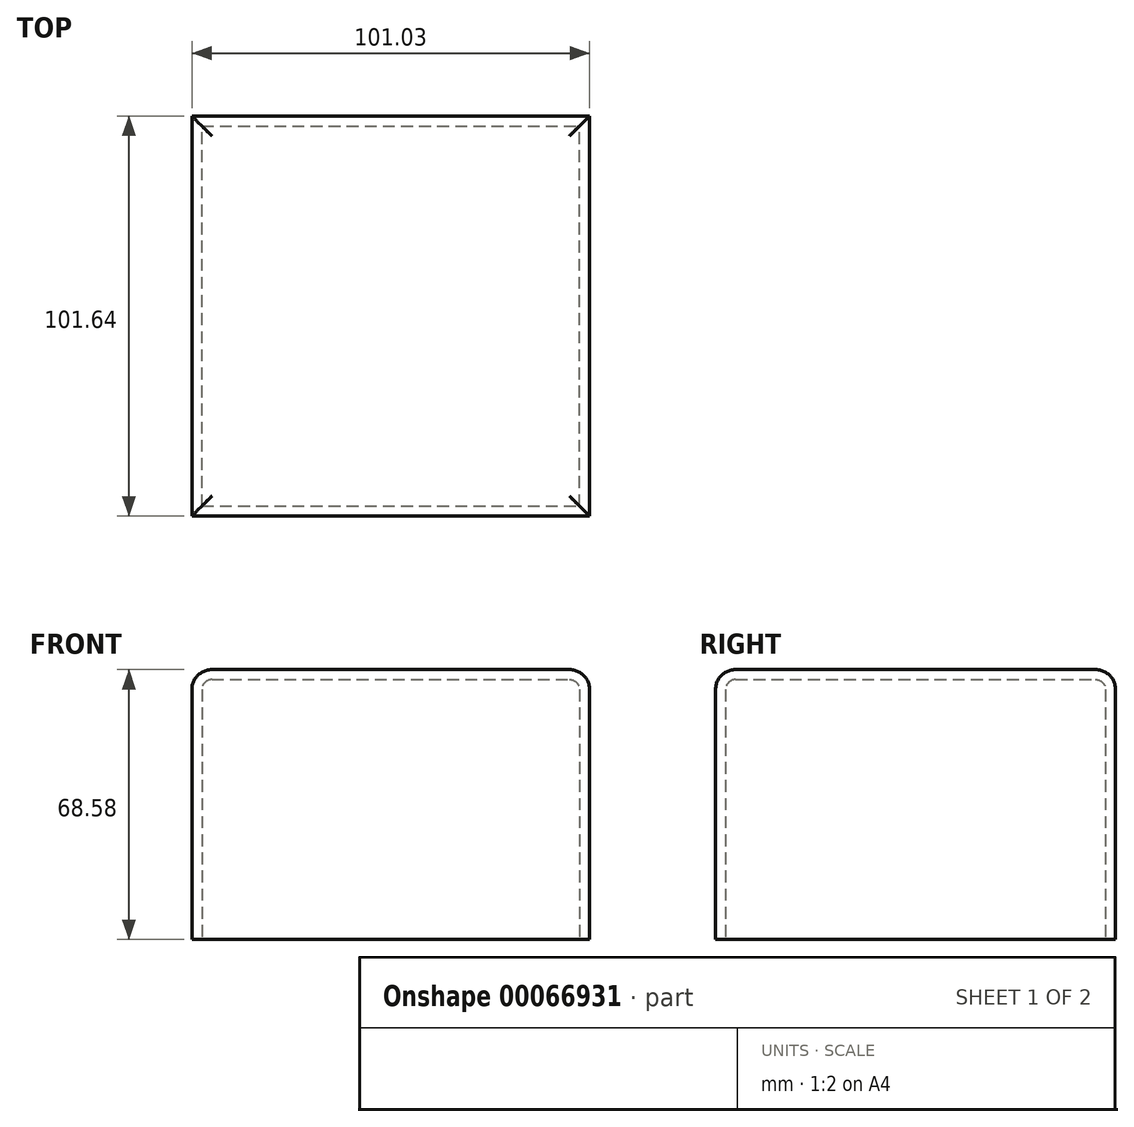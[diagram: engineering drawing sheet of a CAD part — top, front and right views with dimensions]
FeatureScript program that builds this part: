
annotation { "Feature Type Name" : "Feature", "Feature Type Description" : "" }
export const myFeature = defineFeature(function(context is Context, id is Id, definition is map)
    precondition{}
    {
        {
            var Q0;
            Q0=qCreatedBy(makeId("Front.planeOp"),FACE);
            var sketch = newSketch(context, id + "F0", { "sketchPlane" : qUnion([Q0])});
            skLineSegment(sketch, "E0.bottom", {"start": v(-54.37, 59.94) * mm, "end": v(46.66, 59.94) * mm});
            skLineSegment(sketch, "E0.top", {"start": v(-54.37, -8.64) * mm, "end": v(46.66, -8.64) * mm});
            skLineSegment(sketch, "E0.left", {"start": v(-54.37, 59.94) * mm, "end": v(-54.37, -8.64) * mm});
            skLineSegment(sketch, "E0.right", {"start": v(46.66, 59.94) * mm, "end": v(46.66, -8.64) * mm});
            skSolve(sketch);
        }
        {
            var Q0;
            Q0=makeQuery(id+"F0.imprint","IMPRINT",FACE,{"disambiguationData":[TD([[makeQuery(id+"F0.imprint","IMPRINT",EDGE,{"derivedFrom":sQuery(id+"F0.wireOp",EDGE,"E0.bottom")}),-1.0]])]});
            extrude(context, id + "F1", {"entities" : qUnion([Q0]), "depth" : 101.64 * mm});
        }
        {
            var Q0;
            Q0=makeQuery(id+"F1.opExtrude","CAP_EDGE",EDGE,{"disambiguationData":[OSD([sQuery(id+"F0.wireOp",EDGE,"E0.bottom")])],"isStart":false});
            var Q1;
            Q1=makeQuery(id+"F1.opExtrude","SWEPT_EDGE",EDGE,{"disambiguationData":[OSD([sQuery(id+"F0.wireOp",EDGE,"E0.bottom"),sQuery(id+"F0.wireOp",EDGE,"E0.left")])]});
            var Q2;
            Q2=makeQuery(id+"F1.opExtrude","SWEPT_EDGE",EDGE,{"disambiguationData":[OSD([sQuery(id+"F0.wireOp",EDGE,"E0.bottom"),sQuery(id+"F0.wireOp",EDGE,"E0.right")])]});
            var Q3;
            Q3=makeQuery(id+"F1.opExtrude","CAP_EDGE",EDGE,{"disambiguationData":[OSD([sQuery(id+"F0.wireOp",EDGE,"E0.bottom")])],"isStart":true});
            fillet(context, id + "F2", {"entities" : qUnion([Q0, Q1, Q2, Q3]), "radius" : 5.08 * mm, "tangentPropagation" : true, "allowEdgeOverflow" : false});
        }
        {
            var Q0;
            Q0=makeQuery(id+"F1.opExtrude","SWEPT_FACE",FACE,{"disambiguationData":[OSD([sQuery(id+"F0.wireOp",EDGE,"E0.top")])]});
            shell(context, id + "F3", {"entities" : qUnion([Q0]), "thickness" : 2.54 * mm});
        }
    });
